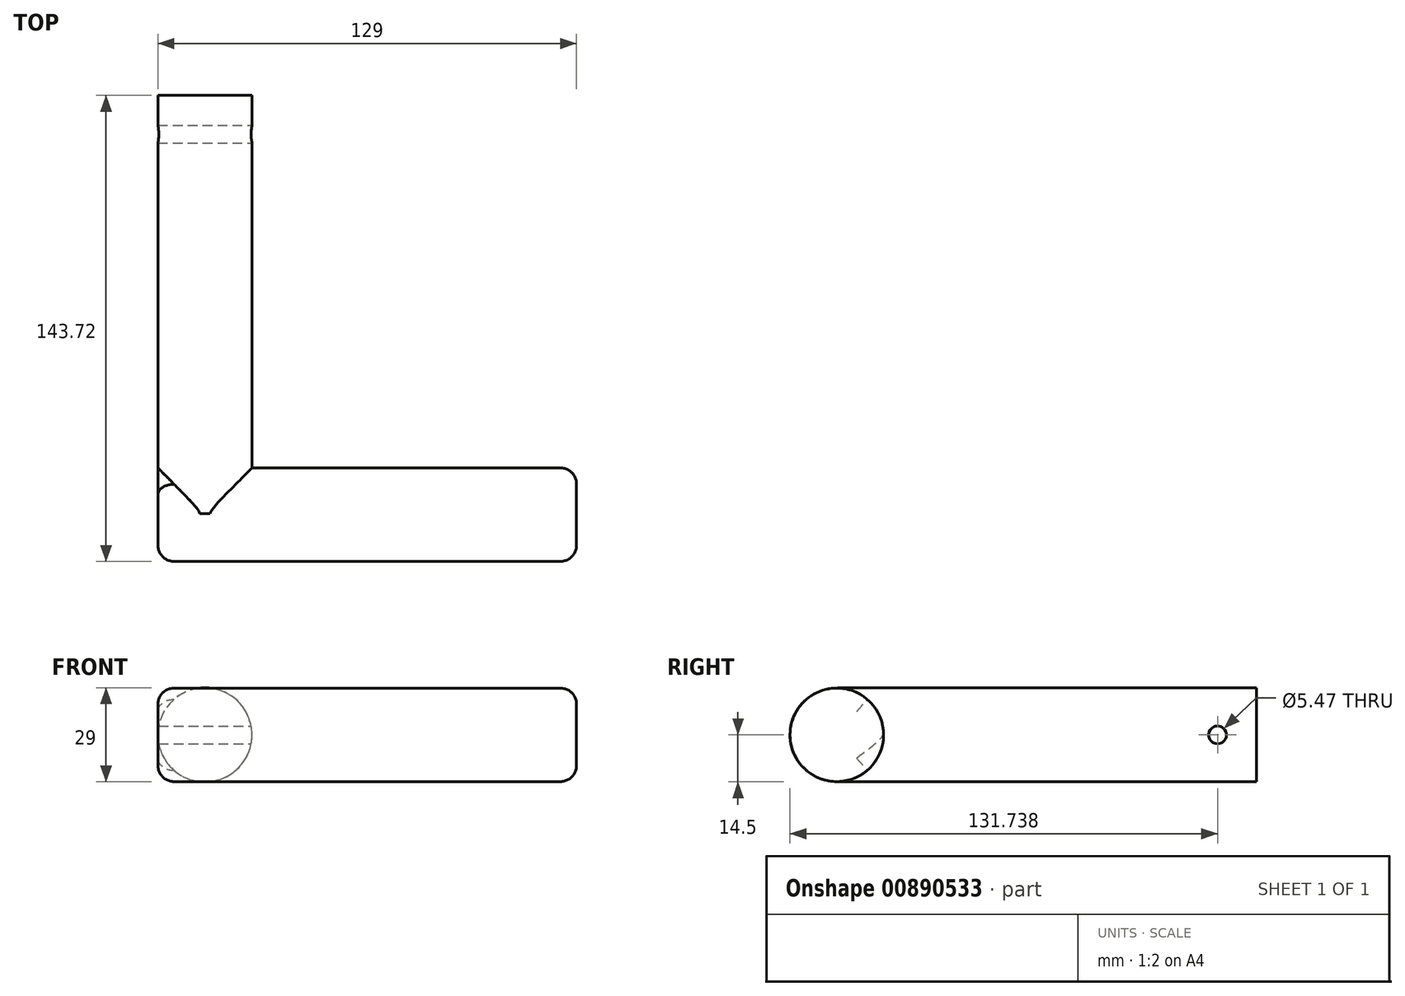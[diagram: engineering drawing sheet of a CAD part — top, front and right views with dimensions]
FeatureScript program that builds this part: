
annotation { "Feature Type Name" : "Feature", "Feature Type Description" : "" }
export const myFeature = defineFeature(function(context is Context, id is Id, definition is map)
    precondition{}
    {
        {
            var Q0;
            Q0=qCreatedBy(makeId("Front.planeOp"),FACE);
            var sketch = newSketch(context, id + "F0", { "sketchPlane" : qUnion([Q0])});
            skCircle(sketch, "E0", {"center": v(0, 0) * mm, "radius": 14.5 * mm});
            skSolve(sketch);
        }
        {
            var Q0;
            Q0 = qSketchRegion(id + "F0", true);
            extrude(context, id + "F1", {"entities" : qUnion([Q0]), "depth" : 129 * mm, "offsetDistance" : 25 * mm});
        }
        {
            var Q0;
            Q0=qCreatedBy(makeId("Right.planeOp"),FACE);
            var sketch = newSketch(context, id + "F2", { "sketchPlane" : qUnion([Q0])});
            skCircle(sketch, "E1", {"center": v(-129.3, 0) * mm, "radius": 14.42 * mm});
            skSolve(sketch);
        }
        {
            var Q0;
            Q0 = qSketchRegion(id + "F2", true);
            extrude(context, id + "F3", {"entities" : qUnion([Q0]), "operationType" : NewBodyOperationType.ADD, "endBound" : BoundingType.SYMMETRIC, "depth" : 29 * mm, "offsetDistance" : 25 * mm});
        }
        {
            var Q0;
            Q0=makeQuery(id+"F3.opExtrude","CAP_FACE",FACE,{"disambiguationData":[OSD([sQuery(id+"F2.wireOp",EDGE,"E1")])],"isStart":false});
            extrude(context, id + "F4", {"entities" : qUnion([Q0]), "operationType" : NewBodyOperationType.ADD, "depth" : 100 * mm, "offsetDistance" : 25 * mm});
        }
        {
            var Q0;
            Q0=qCreatedBy(makeId("Right.planeOp"),FACE);
            var sketch = newSketch(context, id + "F5", { "sketchPlane" : qUnion([Q0])});
            skCircle(sketch, "E2", {"center": v(-11.98, 0) * mm, "radius": 2.73 * mm});
            skSolve(sketch);
        }
        {
            var Q0;
            Q0 = qSketchRegion(id + "F5", true);
            extrude(context, id + "F6", {"entities" : qUnion([Q0]), "operationType" : NewBodyOperationType.REMOVE, "endBound" : BoundingType.SYMMETRIC, "oppositeDirection" : true, "depth" : 29 * mm, "offsetDistance" : 25 * mm});
        }
        {
            var Q0;
            Q0=makeQuery(id+"F3.opExtrude","CAP_EDGE",EDGE,{"disambiguationData":[OSD([sQuery(id+"F2.wireOp",EDGE,"E1")])],"isStart":true});
            var Q1;
            Q1=makeQuery(id+"F4.opExtrude","CAP_FACE",FACE,{"disambiguationData":[OSD([sQuery(id+"F2.wireOp",EDGE,"E1")])],"isStart":false});
            fillet(context, id + "F7", {"entities" : qUnion([Q0, Q1]), "radius" : 5 * mm, "tangentPropagation" : true, "allowEdgeOverflow" : false});
        }
    });
